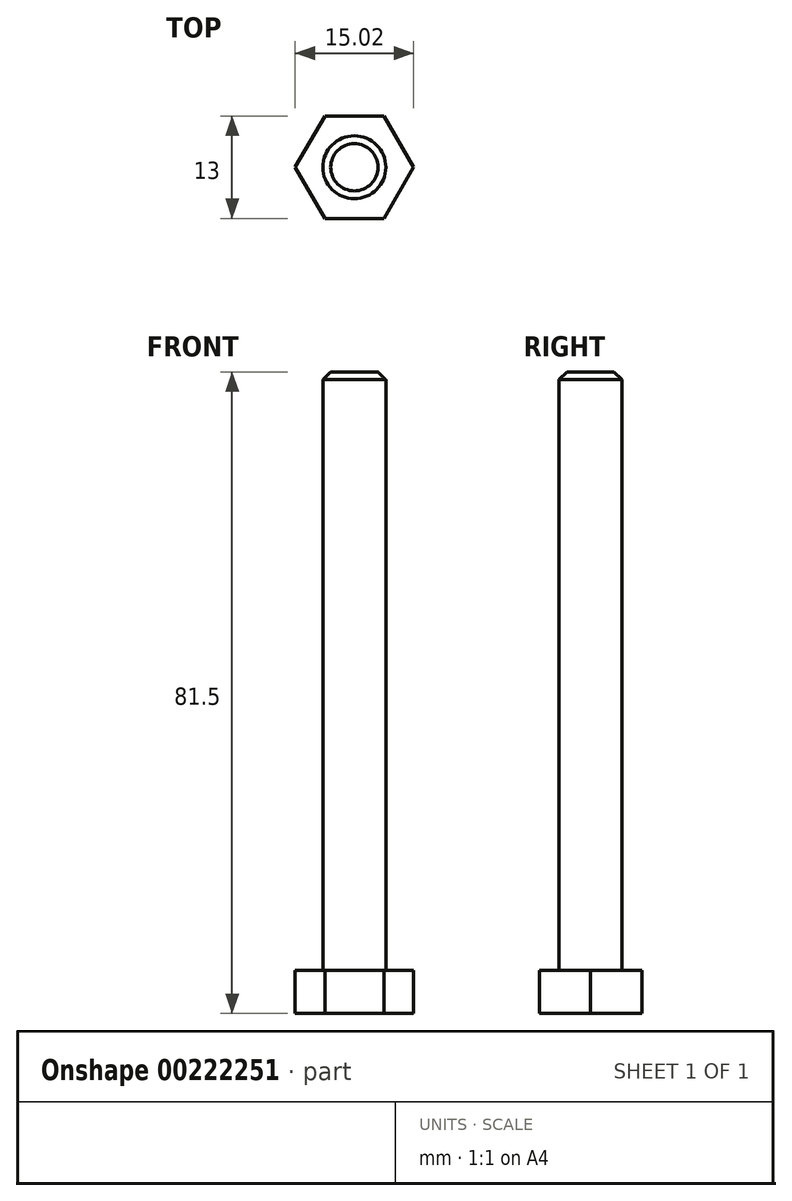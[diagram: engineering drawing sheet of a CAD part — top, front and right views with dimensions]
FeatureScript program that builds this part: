
annotation { "Feature Type Name" : "Feature", "Feature Type Description" : "" }
export const myFeature = defineFeature(function(context is Context, id is Id, definition is map)
    precondition{}
    {
        {
            var Q0;
            Q0=qCreatedBy(makeId("Top.planeOp"),FACE);
            var sketch = newSketch(context, id + "F0", { "sketchPlane" : qUnion([Q0])});
            skCircle(sketch, "E0.cCircle", {"center": v(0, 0) * mm, "radius": 6.5 * mm, "construction": true});
            skLineSegment(sketch, "E0.0", {"start": v(-3.75, 6.5) * mm, "end": v(3.75, 6.5) * mm});
            skLineSegment(sketch, "E0.1", {"start": v(3.75, 6.5) * mm, "end": v(7.5, 0) * mm});
            skLineSegment(sketch, "E0.2", {"start": v(7.5, 0) * mm, "end": v(3.75, -6.5) * mm});
            skLineSegment(sketch, "E0.3", {"start": v(3.75, -6.5) * mm, "end": v(-3.75, -6.5) * mm});
            skLineSegment(sketch, "E0.4", {"start": v(-3.75, -6.5) * mm, "end": v(-7.5, 0) * mm});
            skLineSegment(sketch, "E0.5", {"start": v(-7.5, 0) * mm, "end": v(-3.75, 6.5) * mm});
            skPoint(sketch, "E0.0.midPoint", {"position": v(0, 6.5) * mm});
            skCircle(sketch, "E1", {"center": v(0, 0) * mm, "radius": 4 * mm});
            skSolve(sketch);
        }
        {
            var Q0;
            Q0=makeQuery(id+"F0.imprint","IMPRINT",FACE,{"disambiguationData":[TD([[makeQuery(id+"F0.imprint","IMPRINT",EDGE,{"derivedFrom":sQuery(id+"F0.wireOp",EDGE,"E0.0")}),-1.0]])]});
            var Q1;
            Q1=makeQuery(id+"F0.imprint","IMPRINT",FACE,{"disambiguationData":[TD([[makeQuery(id+"F0.imprint","IMPRINT",EDGE,{"derivedFrom":sQuery(id+"F0.wireOp",EDGE,"E1")}),1.0]])]});
            extrude(context, id + "F1", {"entities" : qUnion([Q0, Q1]), "oppositeDirection" : true, "depth" : 5.5 * mm});
        }
        {
            var Q0;
            Q0=makeQuery(id+"F0.imprint","IMPRINT",FACE,{"disambiguationData":[TD([[makeQuery(id+"F0.imprint","IMPRINT",EDGE,{"derivedFrom":sQuery(id+"F0.wireOp",EDGE,"E1")}),1.0]])]});
            extrude(context, id + "F2", {"entities" : qUnion([Q0]), "operationType" : NewBodyOperationType.ADD, "depth" : 76 * mm});
        }
        {
            var Q0;
            Q0=makeQuery(id+"F0.imprint","IMPRINT",FACE,{"disambiguationData":[TD([[makeQuery(id+"F0.imprint","IMPRINT",EDGE,{"derivedFrom":sQuery(id+"F0.wireOp",EDGE,"E0.0")}),-1.0]])]});
            var Q1;
            Q1=makeQuery(id+"F0.imprint","IMPRINT",FACE,{"disambiguationData":[TD([[makeQuery(id+"F0.imprint","IMPRINT",EDGE,{"derivedFrom":sQuery(id+"F0.wireOp",EDGE,"E1")}),1.0]])]});
            extrude(context, id + "F3", {"entities" : qUnion([Q0, Q1]), "oppositeDirection" : true, "depth" : 5.5 * mm});
        }
        {
            var Q0;
            Q0=makeQuery(id+"F0.imprint","IMPRINT",FACE,{"disambiguationData":[TD([[makeQuery(id+"F0.imprint","IMPRINT",EDGE,{"derivedFrom":sQuery(id+"F0.wireOp",EDGE,"E1")}),1.0]])]});
            extrude(context, id + "F4", {"entities" : qUnion([Q0]), "operationType" : NewBodyOperationType.ADD, "depth" : 68 * mm});
        }
        {
            var Q0;
            Q0=makeQuery(id+"F2.opExtrude","CAP_EDGE",EDGE,{"disambiguationData":[OSD([sQuery(id+"F0.wireOp",EDGE,"E1")])],"isStart":false});
            var Q1;
            Q1=makeQuery(id+"F4.opExtrude","CAP_EDGE",EDGE,{"disambiguationData":[OSD([sQuery(id+"F0.wireOp",EDGE,"E1")])],"isStart":false});
            chamfer(context, id + "F5", {"entities" : qUnion([Q0, Q1]), "width" : 1 * mm, "tangentPropagation" : true});
        }
    });
